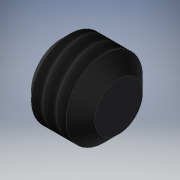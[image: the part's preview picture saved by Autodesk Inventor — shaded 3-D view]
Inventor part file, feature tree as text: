
AUTODESK INVENTOR PART (.ipt)
format: ipt  version: 2019 (Build 230136000, 136)  size: 145,408 bytes
history: native  units: mm
features: other x7, sketch x3, revolve x2, thread x1, extrude x1
ambient origin geometry x8: Origin, YZ Plane, XZ Plane, XY Plane, X Axis, Y Axis, Z Axis, Center Point
bodies: Solid1 (feature_tree)
feature tree (14):
  revolve  "Revolution1"  [1 undecoded]
  thread  "Thread1"  [1 undecoded]
  extrude  "Extrusion1"  TaperAngle=0.0deg  [1 undecoded]
  revolve  "Revolution2"  [1 undecoded]
  other  "CP_XY"
  other  "CP_YZ"
  other  "CP_ZX"
  other  "CP_X"
  other  "CP_Y"
  other  "CP_Z"
  other  "CP_Center"
  sketch  "Sketch_1"  dims[d0=360.0deg d1=1.8205mm d2=0.0mm d3=1.5mm d4=0.0mm]
  sketch  "Sketch_2"  dims[d5=360.0deg d6=0.0mm]
  sketch  "Sketch_3"
note: 4 required parameter values undecoded (feature->parameter linkage not recoverable at this tier; creation-order binding heuristic only, values carry confidence <= 0.55)